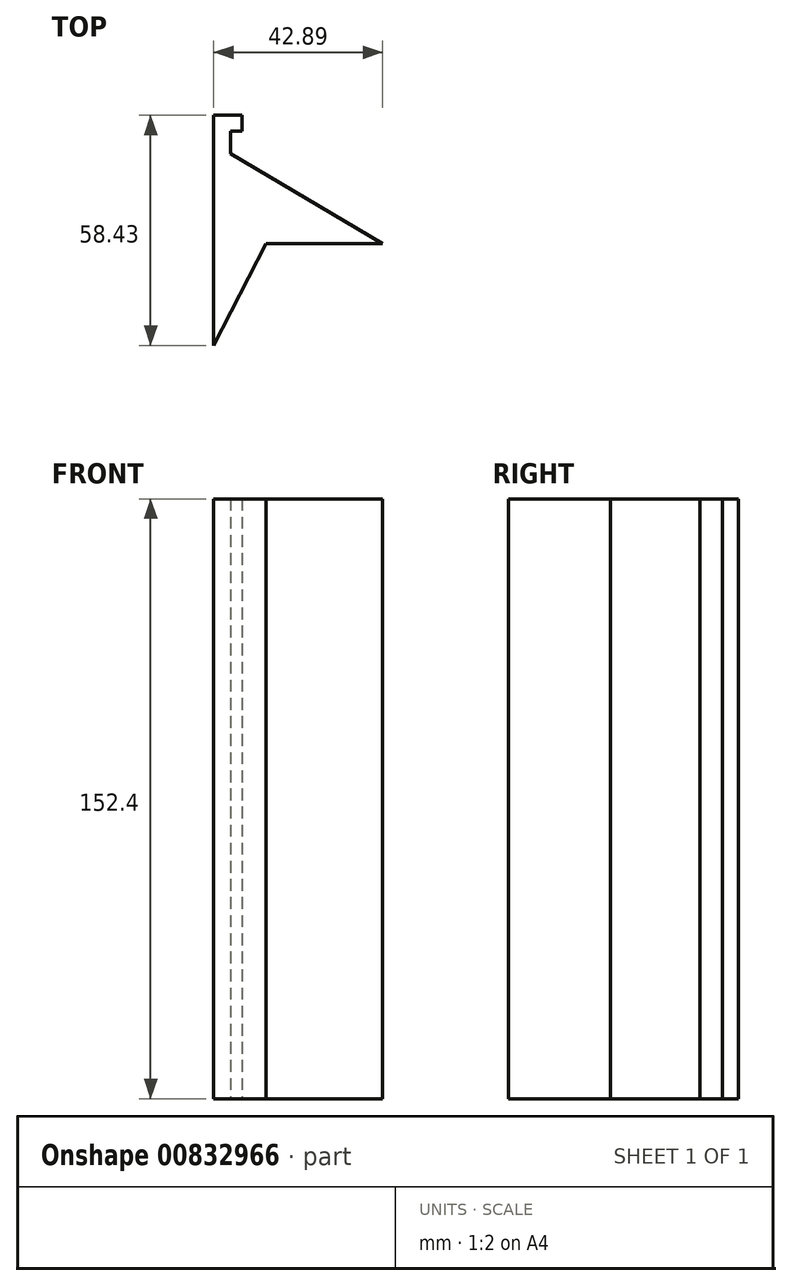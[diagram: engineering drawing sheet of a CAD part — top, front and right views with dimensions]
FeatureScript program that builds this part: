
annotation { "Feature Type Name" : "Feature", "Feature Type Description" : "" }
export const myFeature = defineFeature(function(context is Context, id is Id, definition is map)
    precondition{}
    {
        {
            var Q0;
            Q0=qCreatedBy(makeId("Top.planeOp"),FACE);
            var sketch = newSketch(context, id + "F0", { "sketchPlane" : qUnion([Q0])});
            skLineSegment(sketch, "E0", {"start": v(-31.23, 39.86) * mm, "end": v(-31.23, -11.37) * mm});
            skLineSegment(sketch, "E1", {"start": v(-31.23, -11.37) * mm, "end": v(-17.99, 14.53) * mm});
            skLineSegment(sketch, "E2", {"start": v(-17.99, 14.53) * mm, "end": v(11.66, 14.53) * mm});
            skLineSegment(sketch, "E3", {"start": v(11.66, 14.53) * mm, "end": v(-26.9, 37.31) * mm});
            skPoint(sketch, "E4.end.orphan", {"position": v(-31.23, 14.53) * mm});
            skLineSegment(sketch, "E5", {"start": v(-31.23, 39.86) * mm, "end": v(-31.23, 47.06) * mm});
            skLineSegment(sketch, "E6", {"start": v(-26.9, 43.03) * mm, "end": v(-26.9, 37.31) * mm});
            skLineSegment(sketch, "E7", {"start": v(-26.9, 37.31) * mm, "end": v(-26.9, 43.03) * mm});
            skLineSegment(sketch, "E8", {"start": v(-24.03, 47.06) * mm, "end": v(-24.03, 43.03) * mm});
            skLineSegment(sketch, "E9", {"start": v(-24.03, 43.03) * mm, "end": v(-26.9, 43.03) * mm});
            skPoint(sketch, "E10.end.orphan", {"position": v(-26.9, 47.06) * mm});
            skLineSegment(sketch, "E11", {"start": v(-24.03, 47.06) * mm, "end": v(-31.23, 47.06) * mm});
            skSolve(sketch);
        }
        {
            var Q0;
            Q0=makeQuery(id+"F0.imprint","IMPRINT",FACE,{"disambiguationData":[TD([[makeQuery(id+"F0.imprint","IMPRINT",EDGE,{"derivedFrom":sQuery(id+"F0.wireOp",EDGE,"E0")}),1.0]])]});
            extrude(context, id + "F1", {"entities" : qUnion([Q0]), "depth" : 152.4 * mm, "offsetDistance" : 25.4 * mm});
        }
    });
